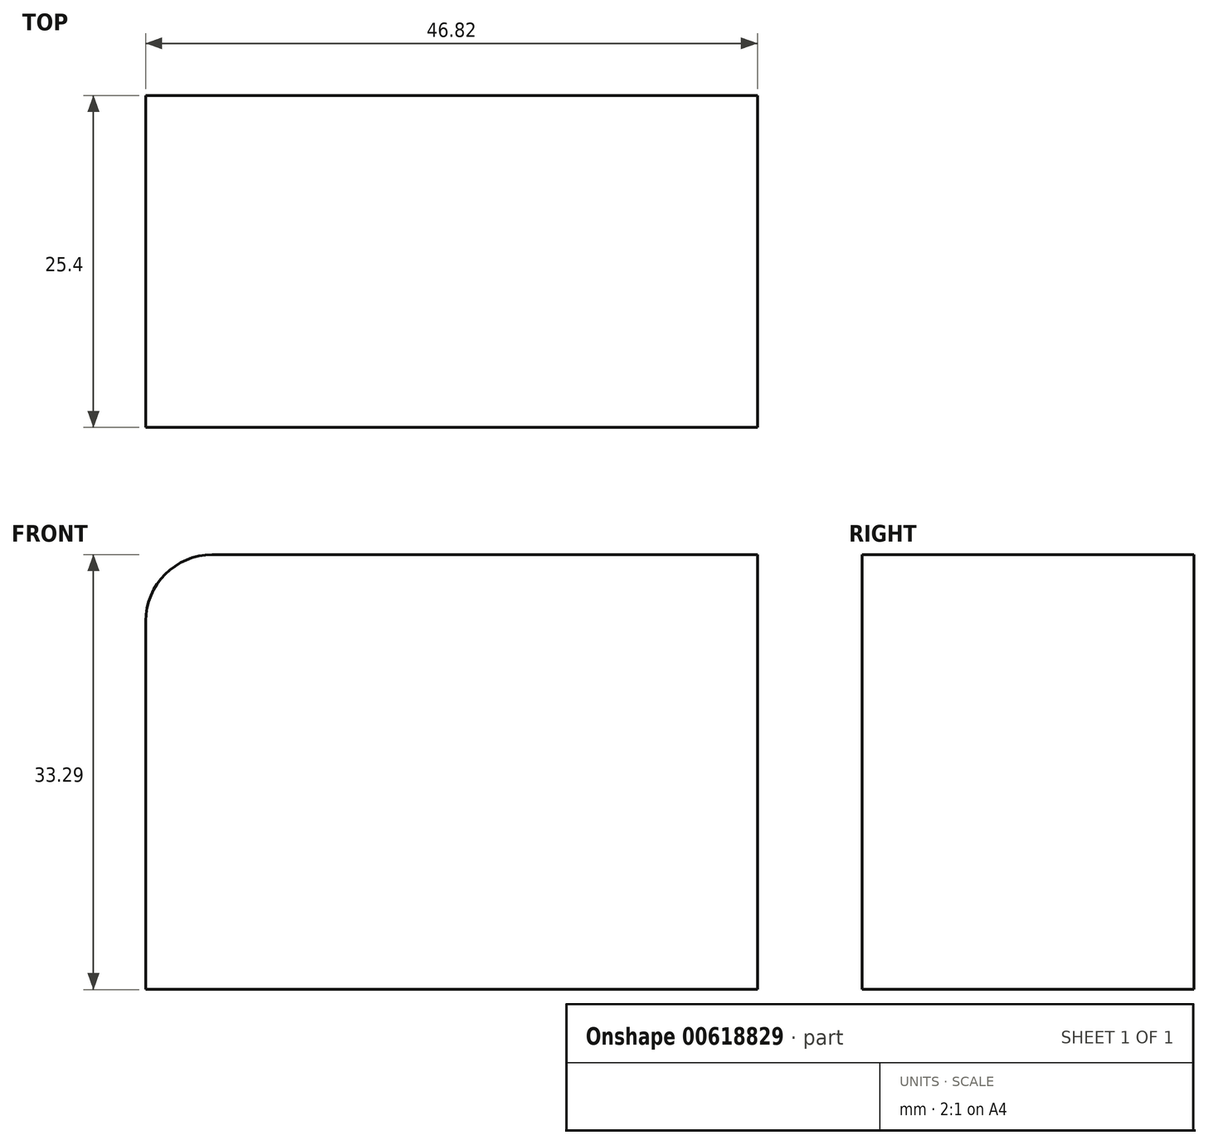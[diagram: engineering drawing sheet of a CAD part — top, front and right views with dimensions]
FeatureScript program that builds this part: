
annotation { "Feature Type Name" : "Feature", "Feature Type Description" : "" }
export const myFeature = defineFeature(function(context is Context, id is Id, definition is map)
    precondition{}
    {
        {
            var Q0;
            Q0=qCreatedBy(makeId("Front.planeOp"),FACE);
            var sketch = newSketch(context, id + "F0", { "sketchPlane" : qUnion([Q0])});
            skLineSegment(sketch, "E0", {"start": v(-65.9, 44.38) * mm, "end": v(-19.09, 44.38) * mm});
            skLineSegment(sketch, "E1", {"start": v(-19.09, 44.38) * mm, "end": v(-19.09, 11.1) * mm});
            skLineSegment(sketch, "E2", {"start": v(-19.09, 11.1) * mm, "end": v(-65.9, 11.1) * mm});
            skLineSegment(sketch, "E3", {"start": v(-65.9, 11.1) * mm, "end": v(-65.9, 44.38) * mm});
            skSolve(sketch);
        }
        {
            var Q0;
            Q0 = qSketchRegion(id + "F0", true);
            extrude(context, id + "F1", {"entities" : qUnion([Q0]), "depth" : 25.4 * mm, "offsetDistance" : 25.4 * mm});
        }
        {
            var Q0;
            Q0=makeQuery(id+"F1.opExtrude","SWEPT_EDGE",EDGE,{"disambiguationData":[OSD([sQuery(id+"F0.wireOp",EDGE,"E0"),sQuery(id+"F0.wireOp",EDGE,"E3")])]});
            fillet(context, id + "F2", {"entities" : qUnion([Q0]), "radius" : 5.08 * mm, "tangentPropagation" : true, "allowEdgeOverflow" : false});
        }
    });
